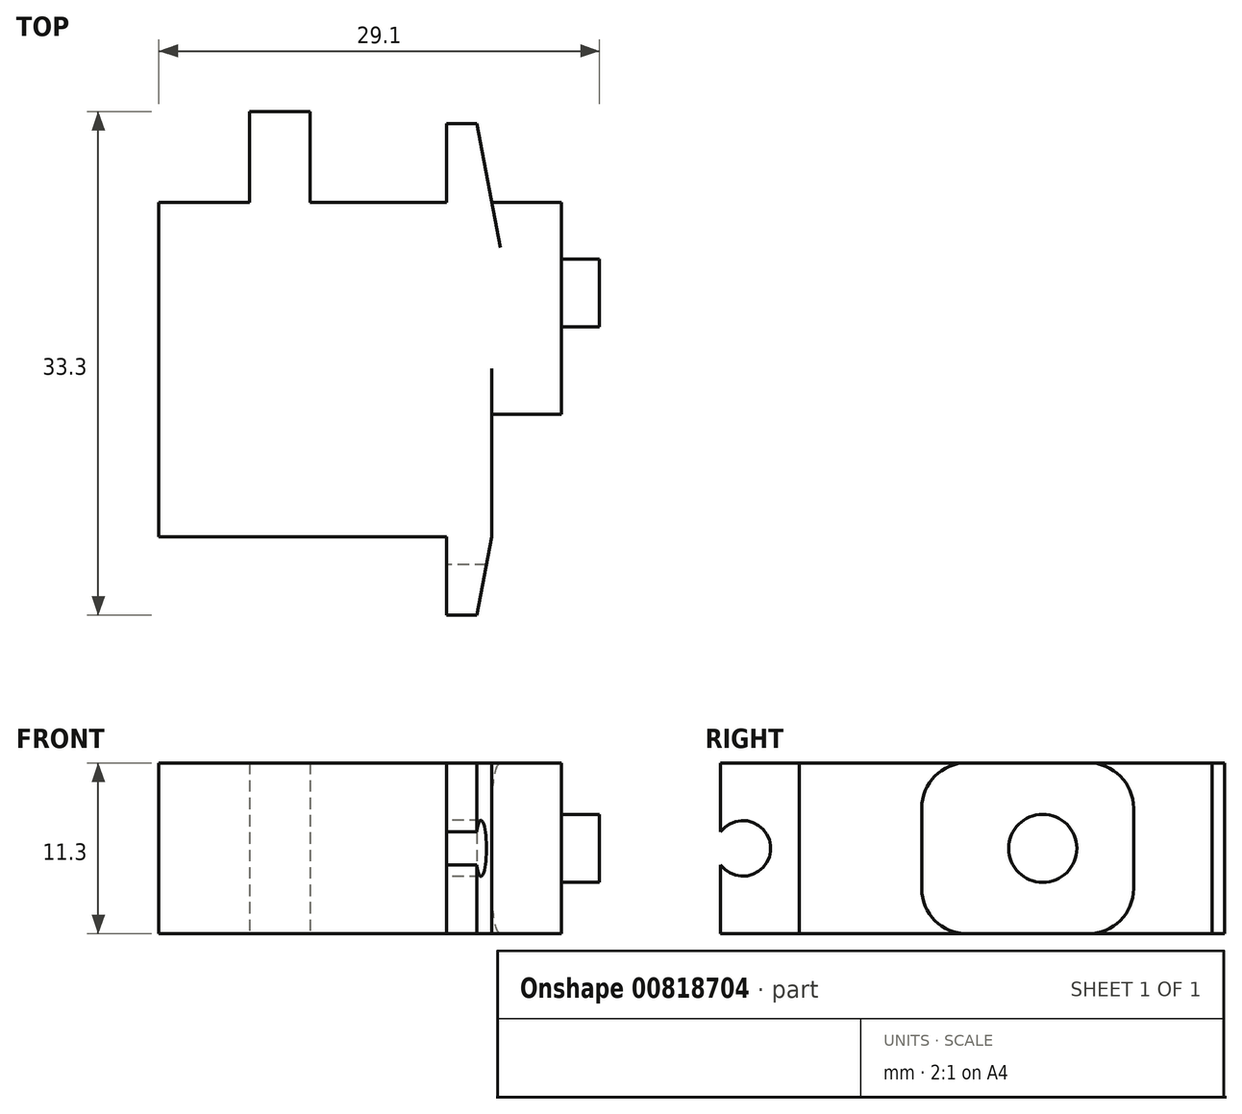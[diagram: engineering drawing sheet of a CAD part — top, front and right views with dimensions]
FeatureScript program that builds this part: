
annotation { "Feature Type Name" : "Feature", "Feature Type Description" : "" }
export const myFeature = defineFeature(function(context is Context, id is Id, definition is map)
    precondition{}
    {
        {
            var Q0;
            Q0=qCreatedBy(makeId("Top.planeOp"),FACE);
            var sketch = newSketch(context, id + "F0", { "sketchPlane" : qUnion([Q0])});
            skLineSegment(sketch, "E0", {"start": v(0, 0) * mm, "end": v(0, 22.1) * mm});
            skLineSegment(sketch, "E1", {"start": v(0, 22.1) * mm, "end": v(6, 22.1) * mm});
            skLineSegment(sketch, "E2", {"start": v(6, 22.1) * mm, "end": v(6, 28.1) * mm});
            skLineSegment(sketch, "E3", {"start": v(6, 28.1) * mm, "end": v(10, 28.1) * mm});
            skLineSegment(sketch, "E4", {"start": v(10, 28.1) * mm, "end": v(10, 22.1) * mm});
            skLineSegment(sketch, "E5", {"start": v(10, 22.1) * mm, "end": v(19, 22.1) * mm});
            skLineSegment(sketch, "E6", {"start": v(19, 22.1) * mm, "end": v(19, 27.3) * mm});
            skLineSegment(sketch, "E7", {"start": v(19, 27.3) * mm, "end": v(21, 27.3) * mm});
            skLineSegment(sketch, "E8", {"start": v(21, 27.3) * mm, "end": v(22, 22.1) * mm});
            skLineSegment(sketch, "E9", {"start": v(22, 22.1) * mm, "end": v(26.6, 22.1) * mm});
            skLineSegment(sketch, "E10", {"start": v(26.6, 22.1) * mm, "end": v(26.6, 8.1) * mm});
            skLineSegment(sketch, "E11", {"start": v(26.6, 8.1) * mm, "end": v(22, 8.1) * mm});
            skLineSegment(sketch, "E12", {"start": v(22, 8.1) * mm, "end": v(22, 0) * mm});
            skLineSegment(sketch, "E13", {"start": v(22, 0) * mm, "end": v(21, -5.2) * mm});
            skLineSegment(sketch, "E14", {"start": v(21, -5.2) * mm, "end": v(19, -5.2) * mm});
            skLineSegment(sketch, "E15", {"start": v(19, -5.2) * mm, "end": v(19, 0) * mm});
            skLineSegment(sketch, "E16", {"start": v(19, 0) * mm, "end": v(0, 0) * mm});
            skSolve(sketch);
        }
        {
            var Q0;
            Q0=makeQuery(id+"F0.imprint","IMPRINT",FACE,{"disambiguationData":[TD([[makeQuery(id+"F0.imprint","IMPRINT",EDGE,{"derivedFrom":sQuery(id+"F0.wireOp",EDGE,"E0")}),-1.0]])]});
            extrude(context, id + "F1", {"entities" : qUnion([Q0]), "depth" : 11.3 * mm, "offsetDistance" : 25 * mm});
        }
        {
            var Q0;
            Q0=makeQuery(id+"F1.opExtrude","CAP_EDGE",EDGE,{"disambiguationData":[OSD([sQuery(id+"F0.wireOp",EDGE,"E11")])],"isStart":true});
            var Q1;
            Q1=makeQuery(id+"F1.opExtrude","CAP_EDGE",EDGE,{"disambiguationData":[OSD([sQuery(id+"F0.wireOp",EDGE,"E11")])],"isStart":false});
            var Q2;
            Q2=makeQuery(id+"F1.opExtrude","CAP_EDGE",EDGE,{"disambiguationData":[OSD([sQuery(id+"F0.wireOp",EDGE,"E9")])],"isStart":false});
            var Q3;
            Q3=makeQuery(id+"F1.opExtrude","CAP_EDGE",EDGE,{"disambiguationData":[OSD([sQuery(id+"F0.wireOp",EDGE,"E9")])],"isStart":true});
            fillet(context, id + "F2", {"entities" : qUnion([Q0, Q1, Q2, Q3]), "tangentPropagation" : true, "radius" : 3 * mm, "defaultsChanged" : true, "vertexSettings" : [], "allowEdgeOverflow" : false});
        }
        {
            var Q0;
            Q0=makeQuery(id+"F1.opExtrude","SWEPT_FACE",FACE,{"disambiguationData":[OSD([sQuery(id+"F0.wireOp",EDGE,"E10")])]});
            var sketch = newSketch(context, id + "F3", { "sketchPlane" : qUnion([Q0])});
            skLineSegment(sketch, "E17", {"start": v(22.1, 5.65) * mm, "end": v(16.1, 5.65) * mm, "construction": true});
            skLineSegment(sketch, "E18.0", {"start": v(0, 11.3) * mm, "end": v(0, 0) * mm});
            skCircle(sketch, "E19", {"center": v(16.1, 5.65) * mm, "radius": 2.25 * mm});
            skSolve(sketch);
        }
        {
            var Q0;
            Q0=makeQuery(id+"F3.imprint","IMPRINT",FACE,{"disambiguationData":[TD([[makeQuery(id+"F3.imprint","IMPRINT",EDGE,{"derivedFrom":sQuery(id+"F3.wireOp",EDGE,"E19")}),1.0]])]});
            extrude(context, id + "F4", {"entities" : qUnion([Q0]), "operationType" : NewBodyOperationType.ADD, "depth" : 2.5 * mm, "offsetDistance" : 25 * mm});
        }
        {
            var Q0;
            Q0=makeQuery(id+"F1.opExtrude","SWEPT_FACE",FACE,{"disambiguationData":[OSD([sQuery(id+"F0.wireOp",EDGE,"E15")])]});
            var sketch = newSketch(context, id + "F5", { "sketchPlane" : qUnion([Q0])});
            skLineSegment(sketch, "E20", {"start": v(5.2, 5.65) * mm, "end": v(0, 5.65) * mm, "construction": true});
            skCircle(sketch, "E21", {"center": v(3.71, 5.65) * mm, "radius": 1.85 * mm});
            skPoint(sketch, "E22", {"position": v(5.2, 6.75) * mm});
            skPoint(sketch, "E23", {"position": v(5.2, 4.55) * mm});
            skLineSegment(sketch, "E24", {"start": v(5.2, 5.65) * mm, "end": v(-27.3, 5.65) * mm, "construction": true});
            skLineSegment(sketch, "E25", {"start": v(-11.05, 5.65) * mm, "end": v(-11.05, 12.08) * mm, "construction": true});
            skCircle(sketch, "E26.MirrorC", {"center": v(-25.81, 5.65) * mm, "radius": 1.85 * mm});
            skLineSegment(sketch, "E27.0", {"start": v(-27.3, 11.3) * mm, "end": v(-27.3, 0) * mm});
            skSolve(sketch);
        }
        {
            var Q0;
            {var subQ0=sQuery(id+"F5.wireOp",EDGE,"E21");var subQ1=makeQuery(id+"F1.opExtrude","SWEPT_EDGE",EDGE,{"disambiguationData":[OSD([sQuery(id+"F0.wireOp",EDGE,"E14"),sQuery(id+"F0.wireOp",EDGE,"E15")])]});var subQ2=makeQuery(id+"F5.imprint","INTERSECT",VERTEX,{"disambiguationData":[OD(0.0)],"derivedFrom":[subQ1,subQ0]});Q0=makeQuery(id+"F5.imprint","IMPRINT",FACE,{"disambiguationData":[TD([[makeQuery(id+"F5.imprint","IMPRINT",EDGE,{"disambiguationData":[TD([[subQ2,1.0]])],"derivedFrom":subQ0}),1.0]])]});}
            var Q1;
            {var subQ0=sQuery(id+"F5.wireOp",EDGE,"E26.MirrorC");var subQ1=sQuery(id+"F5.wireOp",EDGE,"aba32a00-a104-4c46-973c-5d22d6c1dcfa.0");var subQ2=makeQuery(id+"F5.imprint","INTERSECT",VERTEX,{"disambiguationData":[OD(0.0)],"derivedFrom":[subQ1,subQ0]});Q1=makeQuery(id+"F5.imprint","IMPRINT",FACE,{"disambiguationData":[TD([[makeQuery(id+"F5.imprint","IMPRINT",EDGE,{"disambiguationData":[TD([[subQ2,1.0]])],"derivedFrom":subQ1}),1.0]])]});}
            var Q2;
            {var subQ0=sQuery(id+"F5.wireOp",EDGE,"E27.0");var subQ1=sQuery(id+"F5.wireOp",EDGE,"E26.MirrorC");var subQ2=makeQuery(id+"F5.imprint","INTERSECT",VERTEX,{"disambiguationData":[OD(0.0)],"derivedFrom":[subQ1,subQ0]});Q2=makeQuery(id+"F5.imprint","IMPRINT",FACE,{"disambiguationData":[TD([[makeQuery(id+"F5.imprint","IMPRINT",EDGE,{"disambiguationData":[TD([[subQ2,1.0]])],"derivedFrom":subQ1}),-1.0]])]});}
            extrude(context, id + "F6", {"entities" : qUnion([Q0, Q1, Q2]), "operationType" : NewBodyOperationType.REMOVE, "oppositeDirection" : true, "depth" : 25 * mm, "offsetDistance" : 25 * mm});
        }
    });
